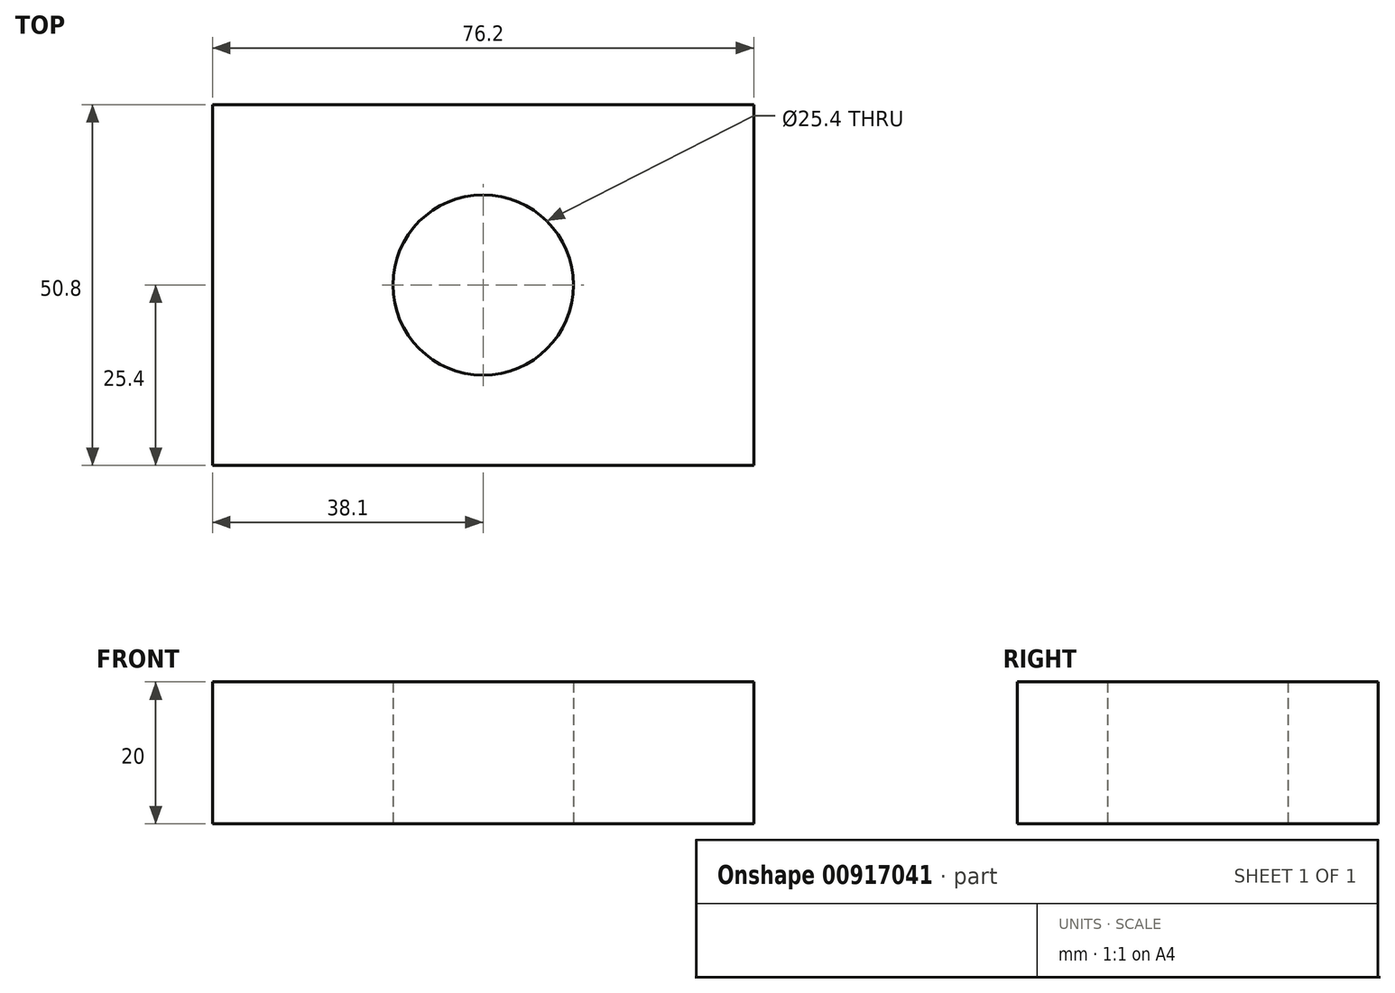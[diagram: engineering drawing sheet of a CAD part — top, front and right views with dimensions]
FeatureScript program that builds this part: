
annotation { "Feature Type Name" : "Feature", "Feature Type Description" : "" }
export const myFeature = defineFeature(function(context is Context, id is Id, definition is map)
    precondition{}
    {
        {
            var Q0;
            Q0=qCreatedBy(makeId("Top.planeOp"),FACE);
            var sketch = newSketch(context, id + "F0", { "sketchPlane" : qUnion([Q0])});
            skLineSegment(sketch, "E0.bottom", {"start": v(38.1, 25.4) * mm, "end": v(-38.1, 25.4) * mm});
            skLineSegment(sketch, "E0.top", {"start": v(38.1, -25.4) * mm, "end": v(-38.1, -25.4) * mm});
            skLineSegment(sketch, "E0.left", {"start": v(38.1, 25.4) * mm, "end": v(38.1, -25.4) * mm});
            skLineSegment(sketch, "E0.right", {"start": v(-38.1, 25.4) * mm, "end": v(-38.1, -25.4) * mm});
            skPoint(sketch, "E0.middle", {"position": v(0, 0) * mm});
            skCircle(sketch, "E1", {"center": v(0, 0) * mm, "radius": 12.7 * mm});
            skSolve(sketch);
        }
        {
            var Q0;
            Q0=makeQuery(id+"F0.imprint","IMPRINT",FACE,{"disambiguationData":[TD([[makeQuery(id+"F0.imprint","IMPRINT",EDGE,{"derivedFrom":sQuery(id+"F0.wireOp",EDGE,"E0.bottom")}),1.0]])]});
            extrude(context, id + "F1", {"entities" : qUnion([Q0]), "depth" : 20 * mm, "offsetDistance" : 25 * mm});
        }
    });
